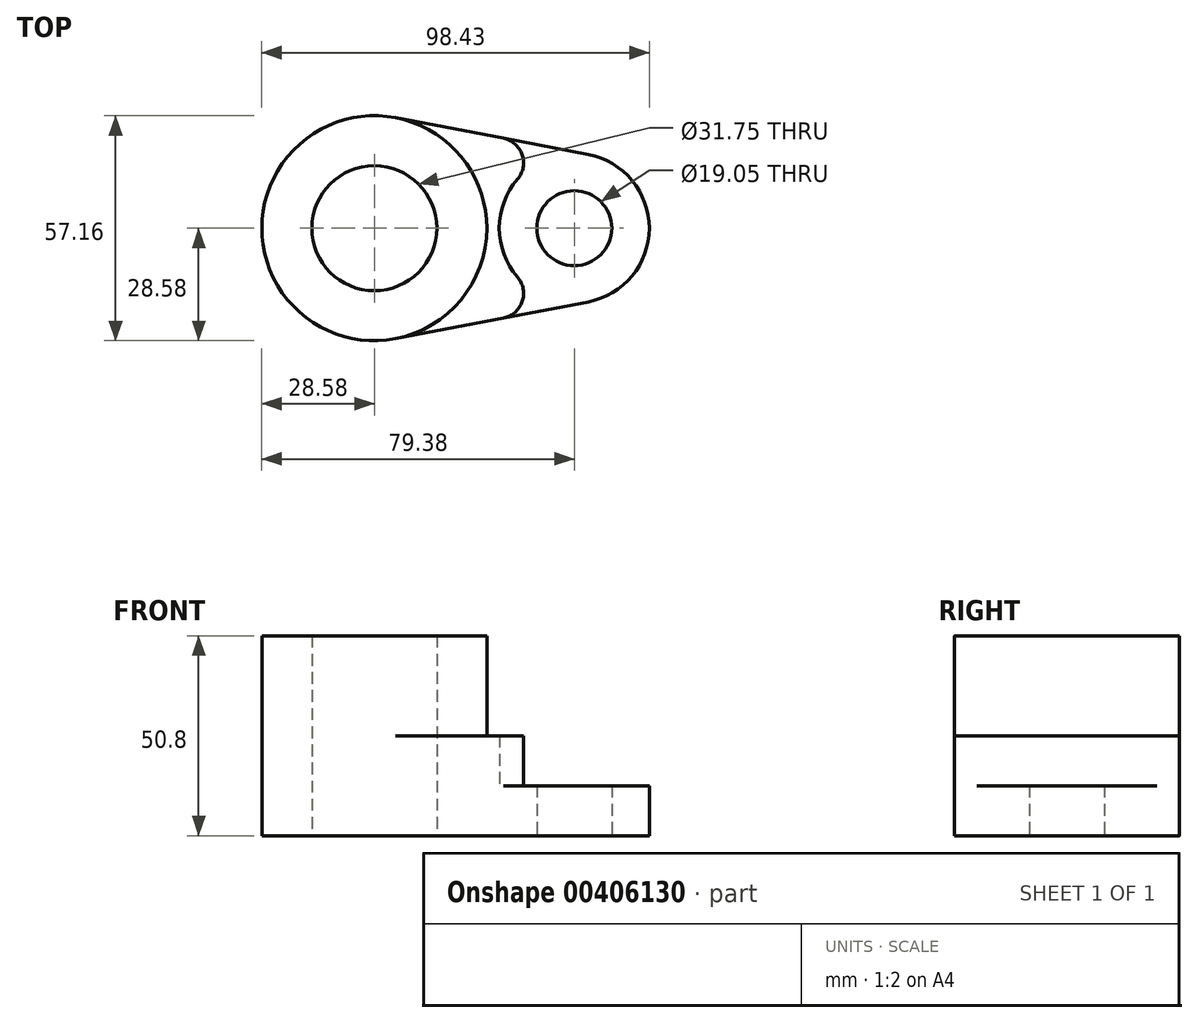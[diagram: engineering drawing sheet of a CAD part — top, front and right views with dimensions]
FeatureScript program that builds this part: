
annotation { "Feature Type Name" : "Feature", "Feature Type Description" : "" }
export const myFeature = defineFeature(function(context is Context, id is Id, definition is map)
    precondition{}
    {
        {
            var Q0;
            Q0=qCreatedBy(makeId("Top.planeOp"),FACE);
            var sketch = newSketch(context, id + "F0", { "sketchPlane" : qUnion([Q0])});
            skCircle(sketch, "E0", {"center": v(0, 0) * mm, "radius": 15.88 * mm});
            skCircle(sketch, "E1", {"center": v(0, 0) * mm, "radius": 28.58 * mm});
            skCircle(sketch, "E2", {"center": v(50.8, 0) * mm, "radius": 19.05 * mm});
            skLineSegment(sketch, "E3", {"start": v(5.36, 28.07) * mm, "end": v(54.37, 18.71) * mm});
            skLineSegment(sketch, "E4", {"start": v(5.36, -28.07) * mm, "end": v(54.37, -18.71) * mm});
            skCircle(sketch, "E5", {"center": v(50.8, 0) * mm, "radius": 9.53 * mm});
            skSolve(sketch);
        }
        {
            var Q0;
            Q0=makeQuery(id+"F0.imprint","IMPRINT",FACE,{"disambiguationData":[TD([[makeQuery(id+"F0.imprint","IMPRINT",EDGE,{"derivedFrom":sQuery(id+"F0.wireOp",EDGE,"E0")}),-1.0]])]});
            extrude(context, id + "F1", {"entities" : qUnion([Q0]), "depth" : 50.8 * mm});
        }
        {
            var Q0;
            {var subQ0=sQuery(id+"F0.wireOp",EDGE,"E3");Q0=makeQuery(id+"F0.imprint","IMPRINT",FACE,{"disambiguationData":[TD([[makeQuery(id+"F0.imprint","IMPRINT",EDGE,{"derivedFrom":subQ0}),-1.0]])]});}
            extrude(context, id + "F2", {"entities" : qUnion([Q0]), "operationType" : NewBodyOperationType.ADD, "depth" : 25.4 * mm});
        }
        {
            var Q0;
            Q0=makeQuery(id+"F0.imprint","IMPRINT",FACE,{"disambiguationData":[TD([[makeQuery(id+"F0.imprint","IMPRINT",EDGE,{"derivedFrom":sQuery(id+"F0.wireOp",EDGE,"E5")}),-1.0]])]});
            extrude(context, id + "F3", {"entities" : qUnion([Q0]), "operationType" : NewBodyOperationType.ADD, "depth" : 12.7 * mm});
        }
        {
            var Q0;
            {var subQ0=sQuery(id+"F0.wireOp",EDGE,"E2");var subQ1=sQuery(id+"F0.wireOp",EDGE,"E4");Q0=makeQuery(id+"F3.boolean.opBoolean","SPLIT",EDGE,{"disambiguationData":[topologyDisambiguationEdgeConnected([makeQuery(id+"F2.opExtrude","SWEPT_FACE",FACE,{"disambiguationData":[OSD([subQ0])]})])],"derivedFrom":makeQuery(id+"F2.opExtrude","SWEPT_EDGE",EDGE,{"disambiguationData":[OSD([subQ0,subQ1])]})});}
            var Q1;
            {var subQ0=sQuery(id+"F0.wireOp",EDGE,"E2");var subQ1=sQuery(id+"F0.wireOp",EDGE,"E3");Q1=makeQuery(id+"F3.boolean.opBoolean","SPLIT",EDGE,{"disambiguationData":[topologyDisambiguationEdgeConnected([makeQuery(id+"F2.opExtrude","SWEPT_FACE",FACE,{"disambiguationData":[OSD([subQ0])]})])],"derivedFrom":makeQuery(id+"F2.opExtrude","SWEPT_EDGE",EDGE,{"disambiguationData":[OSD([subQ0,subQ1])]})});}
            fillet(context, id + "F4", {"entities" : qUnion([Q0, Q1]), "radius" : 6.35 * mm, "tangentPropagation" : true, "allowEdgeOverflow" : false});
        }
    });
